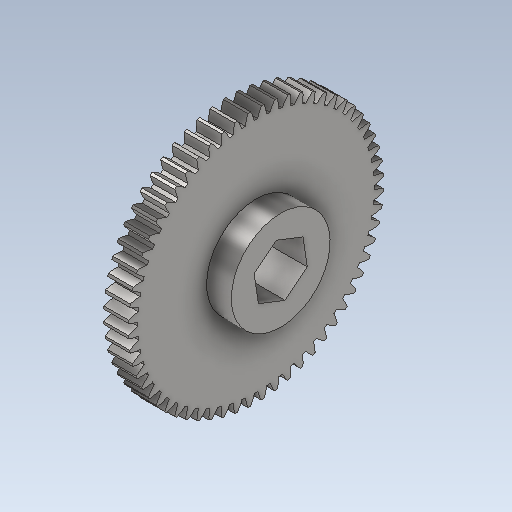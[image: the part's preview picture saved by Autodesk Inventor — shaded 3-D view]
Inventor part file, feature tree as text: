
AUTODESK INVENTOR PART (.ipt)
format: ipt  version: 2023 (Build 270158000, 158)  size: 1,086,976 bytes
history: native  units: in
note: dims shown in document units (in); Inventor stores cm internally (conversion verified against a paired STEP export)
features: sketch x3, projected_geometry x2, revolve x1, extrude x1, hole x1, fillet x1, other x1
ambient origin geometry x8: Origin, YZ Plane, XZ Plane, XY Plane, X Axis, Y Axis, Z Axis, Center Point
bodies: Solid1 (feature_tree)
feature tree (10):
  revolve  "Revolution1"  [1 undecoded]
  extrude  "Extrusion3"  Depth=0.1875in
  hole  "Hole1"  [1 undecoded]
  fillet  "Fillet1"  Radius=0.375in
  sketch  "Sketch3"  dims[d6=0.25in d7=0.1875in]
  projected_geometry  "Projected Loop1"
  sketch  "Sketch4"  dims[d8=0.1875in d10=0.125in]
  projected_geometry  "Projected Loop2"
  sketch  "Sketch5"  dims[d11=90.0deg d12=0.0625in d13=0.13in d14=0.328in d15=0.375in d16=0.25in d17=0.5635in d18=1.0in d19=0.8108in d20=0.375in d21=0.0in d22=0.0in]
  other  "TeethCuts"
note: 2 required parameter values undecoded (feature->parameter linkage not recoverable at this tier; creation-order binding heuristic only, values carry confidence <= 0.55)